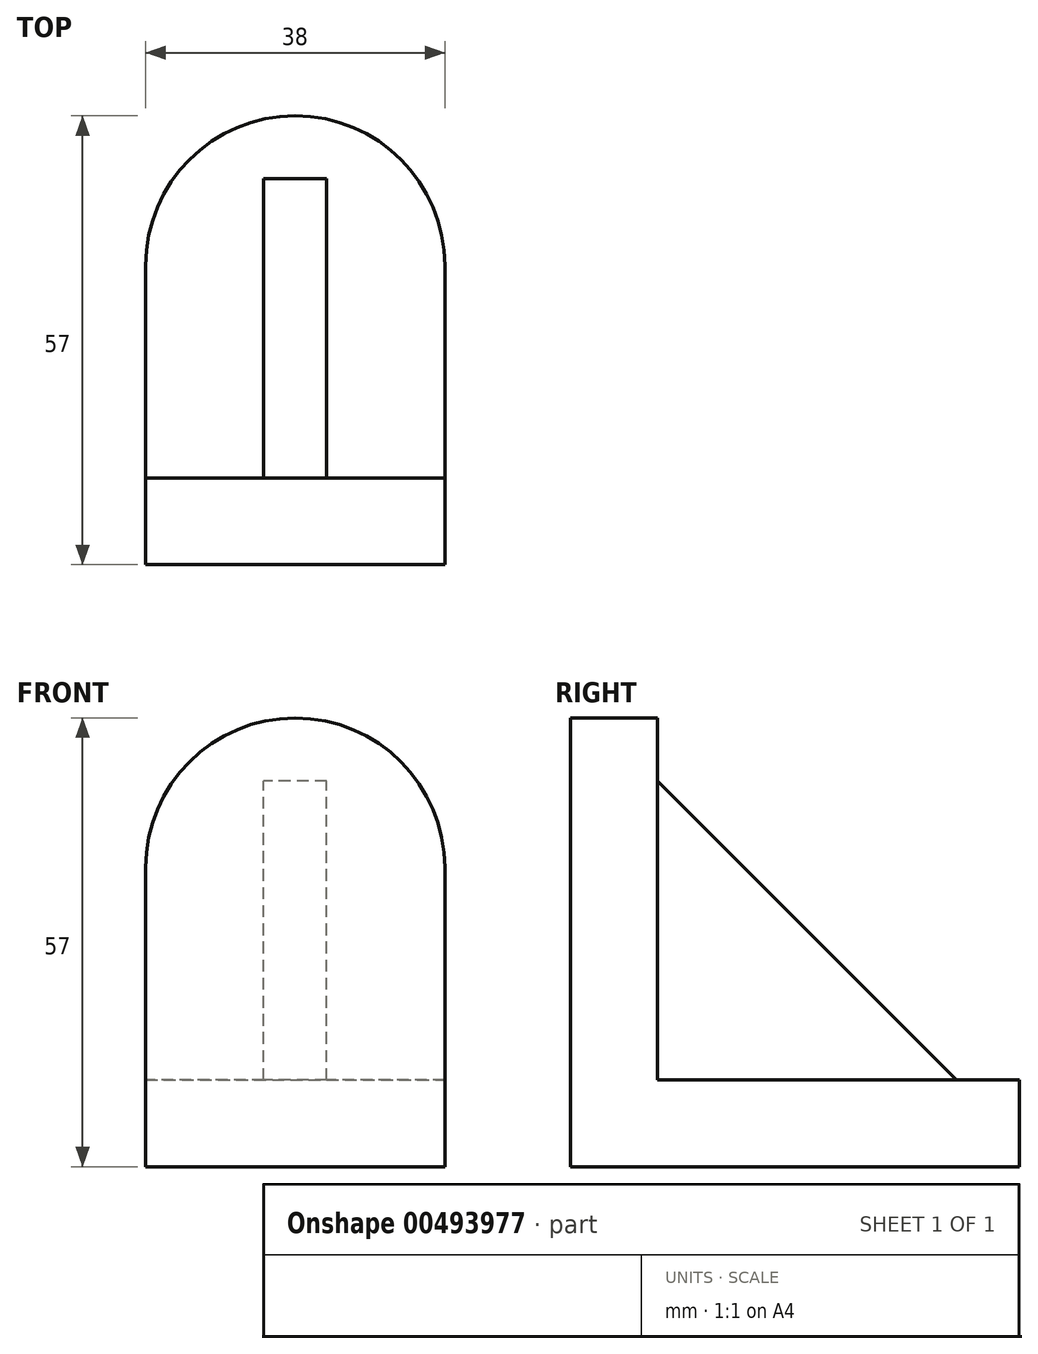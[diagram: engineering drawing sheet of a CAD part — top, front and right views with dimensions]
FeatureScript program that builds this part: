
annotation { "Feature Type Name" : "Feature", "Feature Type Description" : "" }
export const myFeature = defineFeature(function(context is Context, id is Id, definition is map)
    precondition{}
    {
        {
            var Q0;
            Q0=qCreatedBy(makeId("Right.planeOp"),FACE);
            var sketch = newSketch(context, id + "F0", { "sketchPlane" : qUnion([Q0])});
            skLineSegment(sketch, "E0", {"start": v(-14.5, -3.68) * mm, "end": v(42.5, -3.68) * mm});
            skLineSegment(sketch, "E1", {"start": v(42.5, -3.68) * mm, "end": v(42.5, 7.32) * mm});
            skLineSegment(sketch, "E2", {"start": v(42.5, 7.32) * mm, "end": v(-3.5, 7.32) * mm});
            skLineSegment(sketch, "E3", {"start": v(-3.5, 7.32) * mm, "end": v(-3.5, 53.32) * mm});
            skLineSegment(sketch, "E4", {"start": v(-3.5, 53.32) * mm, "end": v(-14.5, 53.32) * mm});
            skLineSegment(sketch, "E5", {"start": v(-14.5, 53.32) * mm, "end": v(-14.5, -3.68) * mm});
            skSolve(sketch);
        }
        {
            var Q0;
            Q0=makeQuery(id+"F0.imprint","IMPRINT",FACE,{"disambiguationData":[TD([[makeQuery(id+"F0.imprint","IMPRINT",EDGE,{"derivedFrom":sQuery(id+"F0.wireOp",EDGE,"E0")}),1.0]])]});
            extrude(context, id + "F1", {"entities" : qUnion([Q0]), "depth" : 38 * mm});
        }
        {
            var Q0;
            Q0=makeQuery(id+"F1.opExtrude","CAP_EDGE",EDGE,{"disambiguationData":[OSD([sQuery(id+"F0.wireOp",EDGE,"E4")])],"isStart":false});
            var Q1;
            Q1=makeQuery(id+"F1.opExtrude","CAP_EDGE",EDGE,{"disambiguationData":[OSD([sQuery(id+"F0.wireOp",EDGE,"E4")])],"isStart":true});
            fillet(context, id + "F2", {"entities" : qUnion([Q0, Q1]), "radius" : 19 * mm, "tangentPropagation" : true, "allowEdgeOverflow" : false});
        }
        {
            var Q0;
            Q0=makeQuery(id+"F1.opExtrude","CAP_EDGE",EDGE,{"disambiguationData":[OSD([sQuery(id+"F0.wireOp",EDGE,"E1")])],"isStart":false});
            var Q1;
            Q1=makeQuery(id+"F1.opExtrude","CAP_EDGE",EDGE,{"disambiguationData":[OSD([sQuery(id+"F0.wireOp",EDGE,"E1")])],"isStart":true});
            fillet(context, id + "F3", {"entities" : qUnion([Q0, Q1]), "radius" : 19 * mm, "tangentPropagation" : true, "allowEdgeOverflow" : false});
        }
        {
            var Q0;
            Q0=qCreatedBy(makeId("Right.planeOp"),FACE);
            cPlane(context, id + "F4", {"entities" : qUnion([Q0]), "cplaneType" : CPlaneType.OFFSET, "offset" : (19 - 4) * mm, "width" : 150 * mm, "height" : 150 * mm});
        }
        {
            var Q0;
            Q0=qCreatedBy(id+"F4.planeOp",FACE);
            var sketch = newSketch(context, id + "F5", { "sketchPlane" : qUnion([Q0])});
            skLineSegment(sketch, "E6", {"start": v(-3.5, 45.32) * mm, "end": v(34.5, 7.32) * mm});
            skLineSegment(sketch, "E7", {"start": v(34.5, 7.32) * mm, "end": v(-3.5, 7.32) * mm});
            skLineSegment(sketch, "E8", {"start": v(-3.5, 7.32) * mm, "end": v(-3.5, 45.32) * mm});
            skSolve(sketch);
        }
        {
            var Q0;
            Q0 = qSketchRegion(id + "F5", true);
            extrude(context, id + "F6", {"entities" : qUnion([Q0]), "operationType" : NewBodyOperationType.ADD, "depth" : 8 * mm});
        }
    });
